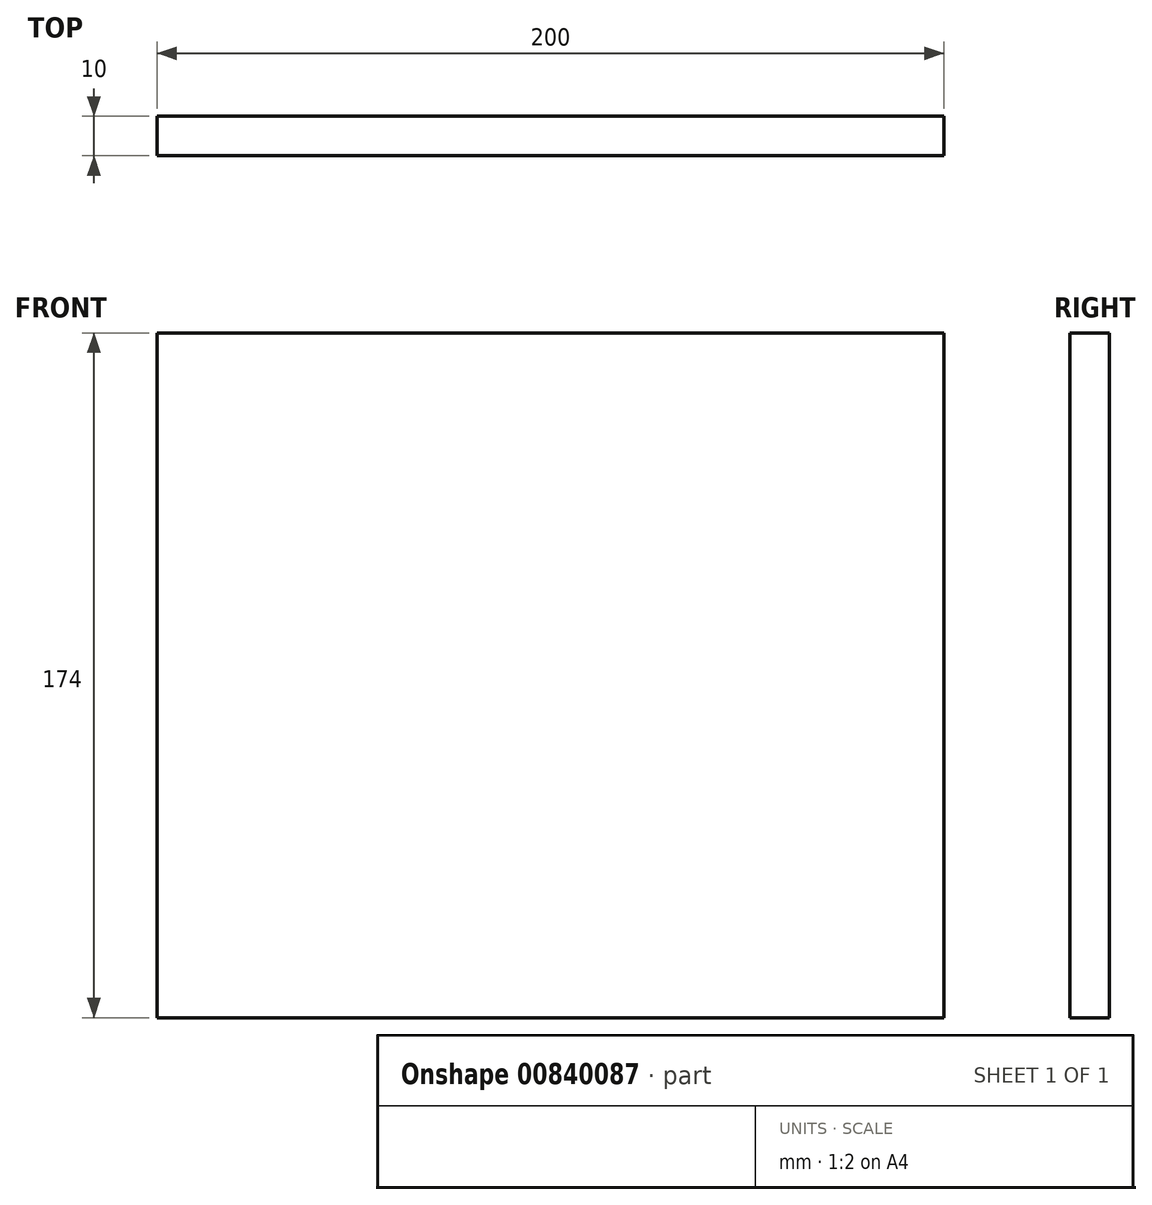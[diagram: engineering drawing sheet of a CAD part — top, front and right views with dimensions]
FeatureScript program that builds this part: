
annotation { "Feature Type Name" : "Feature", "Feature Type Description" : "" }
export const myFeature = defineFeature(function(context is Context, id is Id, definition is map)
    precondition{}
    {
        {
            var Q0;
            Q0=qCreatedBy(makeId("Front.planeOp"),FACE);
            var sketch = newSketch(context, id + "F0", { "sketchPlane" : qUnion([Q0])});
            skLineSegment(sketch, "E0.bottom", {"start": v(0, 0) * mm, "end": v(200, 0) * mm});
            skLineSegment(sketch, "E0.top", {"start": v(0, 174) * mm, "end": v(200, 174) * mm});
            skLineSegment(sketch, "E0.left", {"start": v(0, 0) * mm, "end": v(0, 174) * mm});
            skLineSegment(sketch, "E0.right", {"start": v(200, 0) * mm, "end": v(200, 174) * mm});
            skSolve(sketch);
        }
        {
            var Q0;
            Q0 = qSketchRegion(id + "F0", true);
            extrude(context, id + "F1", {"entities" : qUnion([Q0]), "depth" : 10 * mm, "offsetDistance" : 25 * mm});
        }
    });
